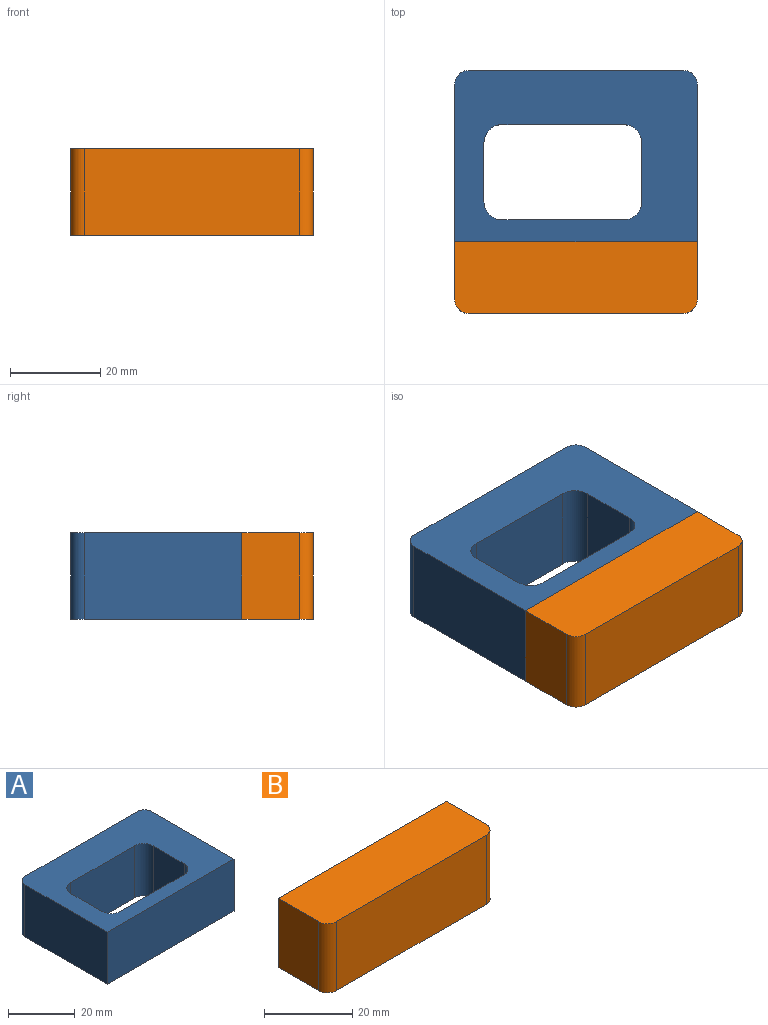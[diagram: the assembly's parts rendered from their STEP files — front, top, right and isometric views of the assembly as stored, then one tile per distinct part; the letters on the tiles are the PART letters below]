
ASSEMBLY  parts=2 mates=1
PART A: 16 faces, bbox 53.9x38x19.2 mm
  f0: plane 53.85x38mm, normal (0,0,1), area 1315.9mm2, adj f2,f3,f4,f5,f6,f7,f8,f9
  f1: plane 53.85x38mm, normal (0,0,-1), area 1315.9mm2, adj f2,f3,f4,f5,f6,f7,f8,f9
  f2: plane 35x19.15mm, normal (-1,0,0), area 670.2mm2, adj f0,f1,f3,f11
  f3: plane 53.85x19.15mm, normal (0,-1,0), area 1031.2mm2, adj f0,f1,f2,f4
  f4: plane 35x19.15mm, normal (1,0,0), area 670.2mm2, adj f0,f1,f3,f10
  f5: plane 47.85x19.15mm, normal (0,1,0), area 916.3mm2, adj f0,f1,f10,f11
  f6: plane 27x19.15mm, normal (0,-1,0), area 517mm2, adj f0,f1,f12,f15
  f7: plane 19.15x13.15mm, normal (1,0,0), area 251.8mm2, adj f0,f1,f12,f13
  f8: plane 27x19.15mm, normal (0,1,0), area 517mm2, adj f0,f1,f13,f14
  f9: plane 19.15x13.15mm, normal (-1,0,0), area 251.8mm2, adj f0,f1,f14,f15
  f10: cylinder r=3mm len=19.15mm, axis (0,0,1), area 90.2mm2, adj f0,f1,f4,f5
  f11: cylinder r=3mm len=19.15mm, axis (0,0,-1), area 90.2mm2, adj f0,f1,f2,f5
  f12: cylinder r=4mm len=19.15mm, axis (0,0,1), area 120.3mm2, adj f0,f1,f6,f7
  f13: cylinder r=4mm len=19.15mm, axis (0,0,-1), area 120.3mm2, adj f0,f1,f7,f8
  f14: cylinder r=4mm len=19.15mm, axis (0,0,1), area 120.3mm2, adj f0,f1,f8,f9
  f15: cylinder r=4mm len=19.15mm, axis (0,0,-1), area 120.3mm2, adj f0,f1,f6,f9
PART B: 8 faces, bbox 53.9x15.9x19.2 mm
  f0: plane 19.15x12.85mm, normal (-1,0,0), area 246.1mm2, adj f3,f4,f5,f6
  f1: plane 47.85x19.15mm, normal (0,-1,0), area 916.3mm2, adj f4,f5,f6,f7
  f2: plane 19.15x12.85mm, normal (1,0,0), area 246.1mm2, adj f3,f4,f5,f7
  f3: plane 53.85x19.15mm, normal (0,1,0), area 1031.2mm2, adj f0,f2,f4,f5
  f4: plane 53.85x15.85mm, normal (0,0,1), area 849.7mm2, adj f0,f1,f2,f3,f6,f7
  f5: plane 53.85x15.85mm, normal (0,0,-1), area 849.7mm2, adj f0,f1,f2,f3,f6,f7
  f6: cylinder r=3mm len=19.15mm, axis (0,0,1), area 90.2mm2, adj f0,f1,f4,f5
  f7: cylinder r=3mm len=19.15mm, axis (0,0,-1), area 90.2mm2, adj f1,f2,f4,f5
PLACE A t=(0.6,11.03,6.45)mm
PLACE B t=(0.6,-15.9,6.45)mm
MATE planar B.f3 <-> A.f3  axis (0,1,0) through (27.53,-7.97,6.45)mm
